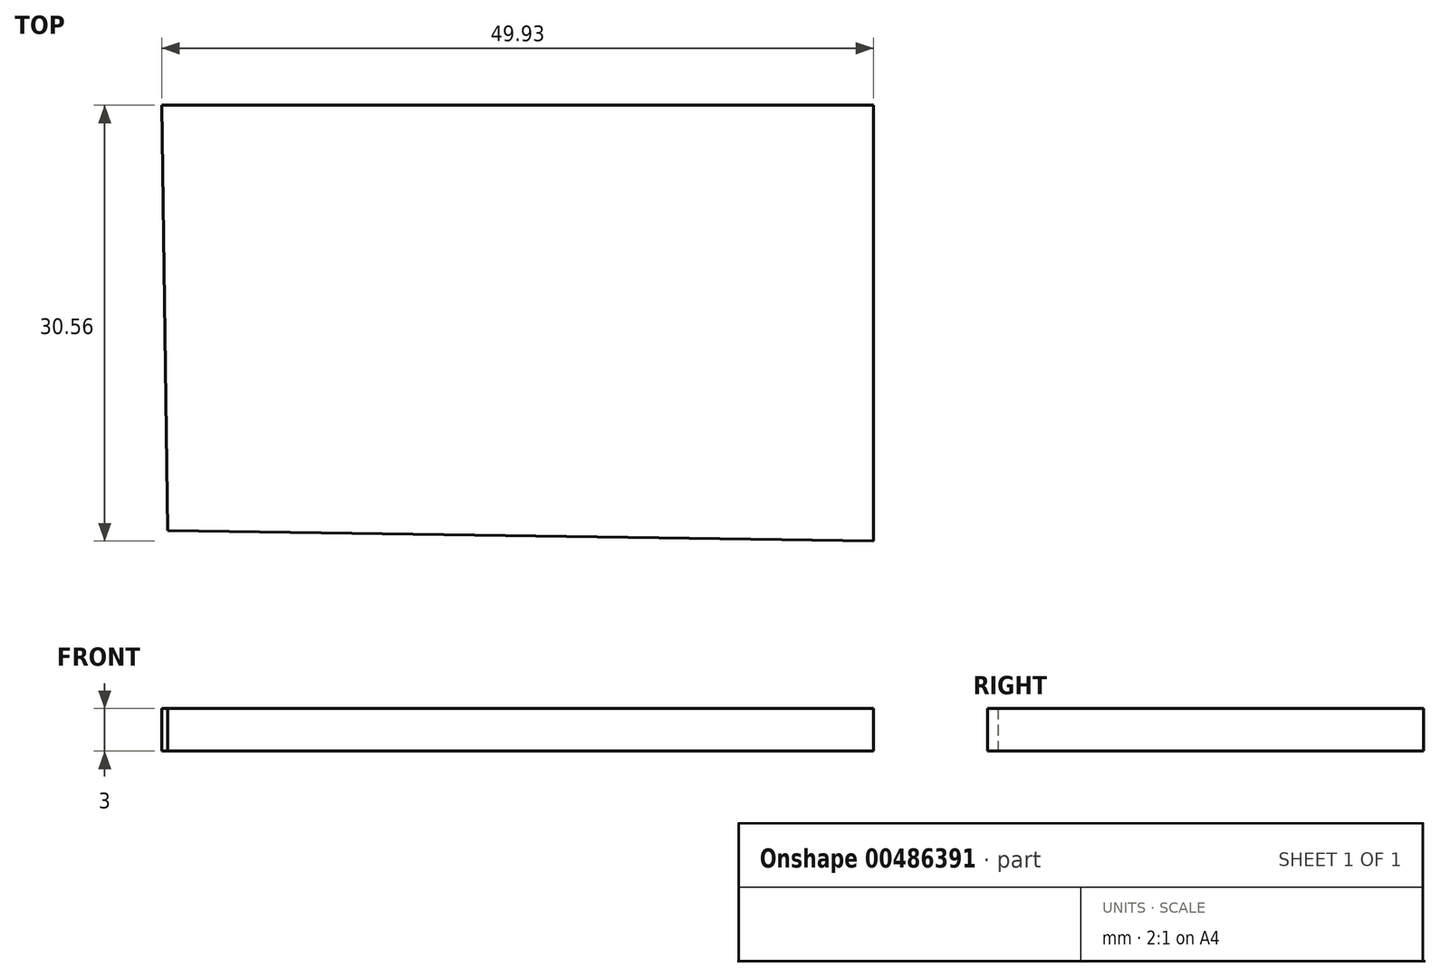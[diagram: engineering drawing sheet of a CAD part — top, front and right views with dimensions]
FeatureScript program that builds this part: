
annotation { "Feature Type Name" : "Feature", "Feature Type Description" : "" }
export const myFeature = defineFeature(function(context is Context, id is Id, definition is map)
    precondition{}
    {
        {
            var Q0;
            Q0=qCreatedBy(makeId("Top.planeOp"),FACE);
            var sketch = newSketch(context, id + "F0", { "sketchPlane" : qUnion([Q0])});
            skLineSegment(sketch, "E0", {"start": v(-8.78, 8.65) * mm, "end": v(41.15, 8.65) * mm});
            skLineSegment(sketch, "E1", {"start": v(41.15, 8.65) * mm, "end": v(41.15, -21.91) * mm});
            skLineSegment(sketch, "E2", {"start": v(41.15, -21.91) * mm, "end": v(-8.34, -21.2) * mm});
            skLineSegment(sketch, "E3", {"start": v(-8.34, -21.2) * mm, "end": v(-8.78, 8.65) * mm});
            skSolve(sketch);
        }
        {
            var Q0;
            Q0=makeQuery(id+"F0.imprint","IMPRINT",FACE,{"disambiguationData":[TD([[makeQuery(id+"F0.imprint","IMPRINT",EDGE,{"derivedFrom":sQuery(id+"F0.wireOp",EDGE,"E0")}),-1.0]])]});
            extrude(context, id + "F1", {"entities" : qUnion([Q0]), "depth" : 3 * mm, "offsetDistance" : 25 * mm});
        }
    });
